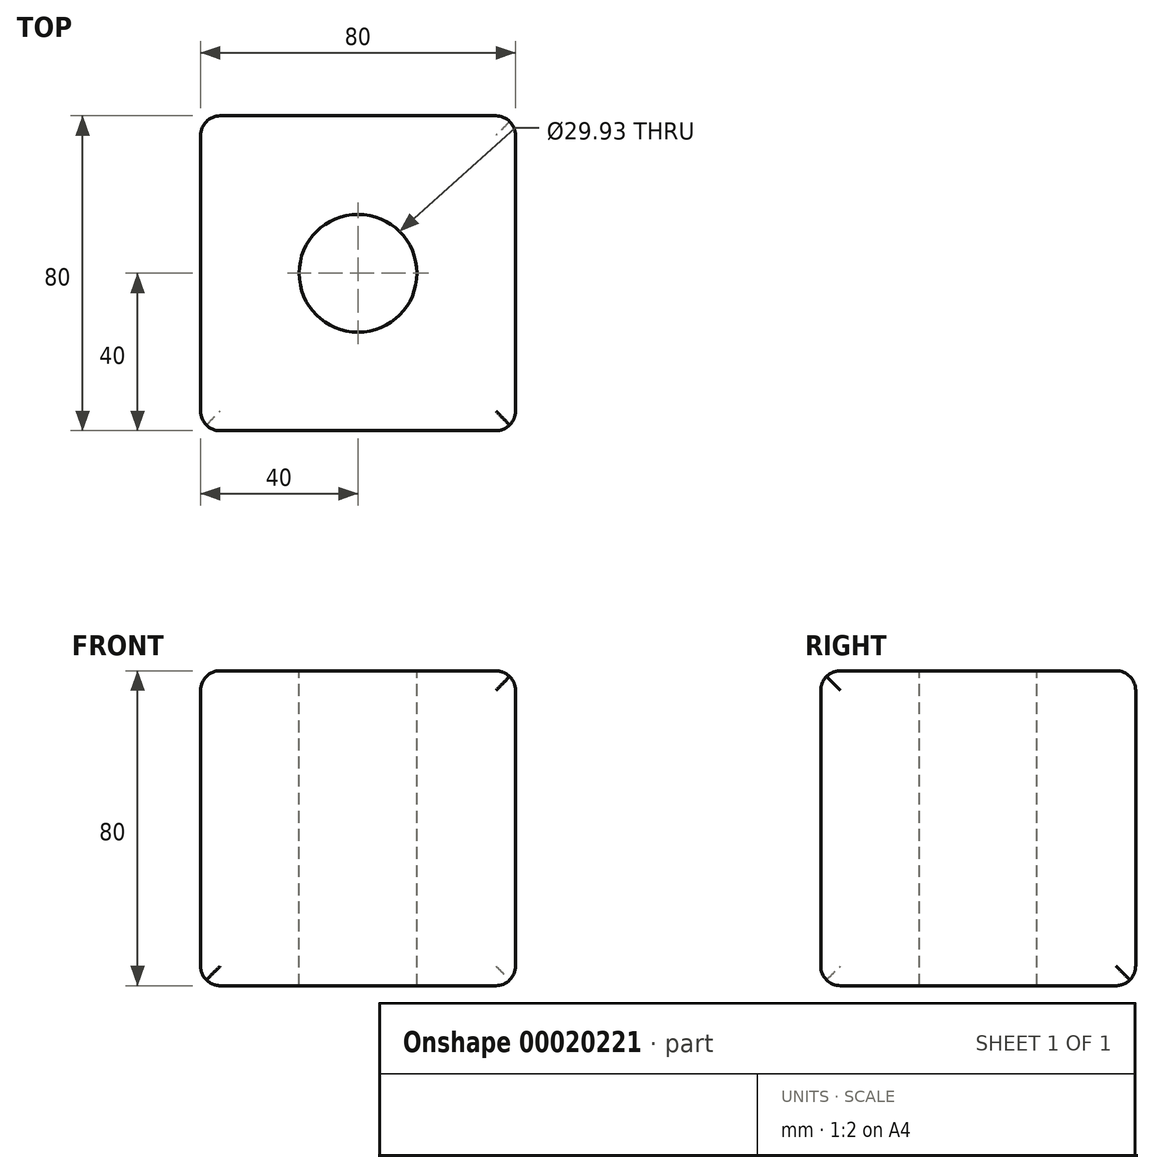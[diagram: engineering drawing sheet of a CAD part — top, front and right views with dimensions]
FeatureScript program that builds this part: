
annotation { "Feature Type Name" : "Feature", "Feature Type Description" : "" }
export const myFeature = defineFeature(function(context is Context, id is Id, definition is map)
    precondition{}
    {
        {
            var Q0;
            Q0=qCreatedBy(makeId("Top.planeOp"),FACE);
            var sketch = newSketch(context, id + "F0", { "sketchPlane" : qUnion([Q0])});
            skLineSegment(sketch, "E0.rect.bottom", {"start": v(40, -40) * mm, "end": v(-40, -40) * mm});
            skLineSegment(sketch, "E0.rect.top", {"start": v(40, 40) * mm, "end": v(-40, 40) * mm});
            skLineSegment(sketch, "E0.rect.left", {"start": v(40, -40) * mm, "end": v(40, 40) * mm});
            skLineSegment(sketch, "E0.rect.right", {"start": v(-40, -40) * mm, "end": v(-40, 40) * mm});
            skPoint(sketch, "E0.rect.middle", {"position": v(0, 0) * mm});
            skSolve(sketch);
        }
        {
            var Q0;
            Q0=makeQuery(id+"F0.imprint","IMPRINT",FACE,{"disambiguationData":[TD([[makeQuery(id+"F0.imprint","IMPRINT",EDGE,{"derivedFrom":sQuery(id+"F0.wireOp",EDGE,"E0.rect.bottom")}),-1.0]])]});
            extrude(context, id + "F1", {"entities" : qUnion([Q0]), "endBound" : BoundingType.SYMMETRIC, "depth" : 80 * mm});
        }
        {
            var Q0;
            Q0=makeQuery(id+"F1.opExtrude","CAP_FACE",FACE,{"disambiguationData":[OSD([sQuery(id+"F0.wireOp",EDGE,"E0.rect.bottom"),sQuery(id+"F0.wireOp",EDGE,"E0.rect.top"),sQuery(id+"F0.wireOp",EDGE,"E0.rect.left"),sQuery(id+"F0.wireOp",EDGE,"E0.rect.right")])],"isStart":false});
            var Q1;
            Q1=makeQuery(id+"F1.opExtrude","SWEPT_FACE",FACE,{"disambiguationData":[OSD([sQuery(id+"F0.wireOp",EDGE,"E0.rect.right")])]});
            var Q2;
            Q2=makeQuery(id+"F1.opExtrude","SWEPT_FACE",FACE,{"disambiguationData":[OSD([sQuery(id+"F0.wireOp",EDGE,"E0.rect.top")])]});
            fillet(context, id + "F2", {"entities" : qUnion([Q0, Q1, Q2]), "radius" : 5 * mm, "tangentPropagation" : true, "allowEdgeOverflow" : false});
        }
        {
            var Q0;
            Q0=makeQuery(id+"F1.opExtrude","SWEPT_FACE",FACE,{"disambiguationData":[OSD([sQuery(id+"F0.wireOp",EDGE,"E0.rect.left")])]});
            var Q1;
            Q1=makeQuery(id+"F1.opExtrude","SWEPT_EDGE",EDGE,{"disambiguationData":[OSD([sQuery(id+"F0.wireOp",EDGE,"E0.rect.bottom"),sQuery(id+"F0.wireOp",EDGE,"E0.rect.left")])]});
            var Q2;
            Q2=makeQuery(id+"F1.opExtrude","SWEPT_FACE",FACE,{"disambiguationData":[OSD([sQuery(id+"F0.wireOp",EDGE,"E0.rect.bottom")])]});
            fillet(context, id + "F3", {"entities" : qUnion([Q0, Q1, Q2]), "radius" : 5 * mm, "allowEdgeOverflow" : false});
        }
        {
            var Q0;
            Q0=makeQuery(id+"F1.opExtrude","CAP_FACE",FACE,{"disambiguationData":[OSD([sQuery(id+"F0.wireOp",EDGE,"E0.rect.bottom"),sQuery(id+"F0.wireOp",EDGE,"E0.rect.top"),sQuery(id+"F0.wireOp",EDGE,"E0.rect.left"),sQuery(id+"F0.wireOp",EDGE,"E0.rect.right")])],"isStart":false});
            var sketch = newSketch(context, id + "F4", { "sketchPlane" : qUnion([Q0])});
            skCircle(sketch, "E1", {"center": v(0, 0) * mm, "radius": 14.96 * mm});
            skSolve(sketch);
        }
        {
            var Q0;
            Q0=makeQuery(id+"F4.imprint","IMPRINT",FACE,{"disambiguationData":[TD([[makeQuery(id+"F4.imprint","IMPRINT",EDGE,{"derivedFrom":sQuery(id+"F4.wireOp",EDGE,"E1")}),1.0]])]});
            extrude(context, id + "F5", {"entities" : qUnion([Q0]), "operationType" : NewBodyOperationType.REMOVE, "endBound" : BoundingType.THROUGH_ALL, "oppositeDirection" : true, "depth" : 25 * mm});
        }
    });
